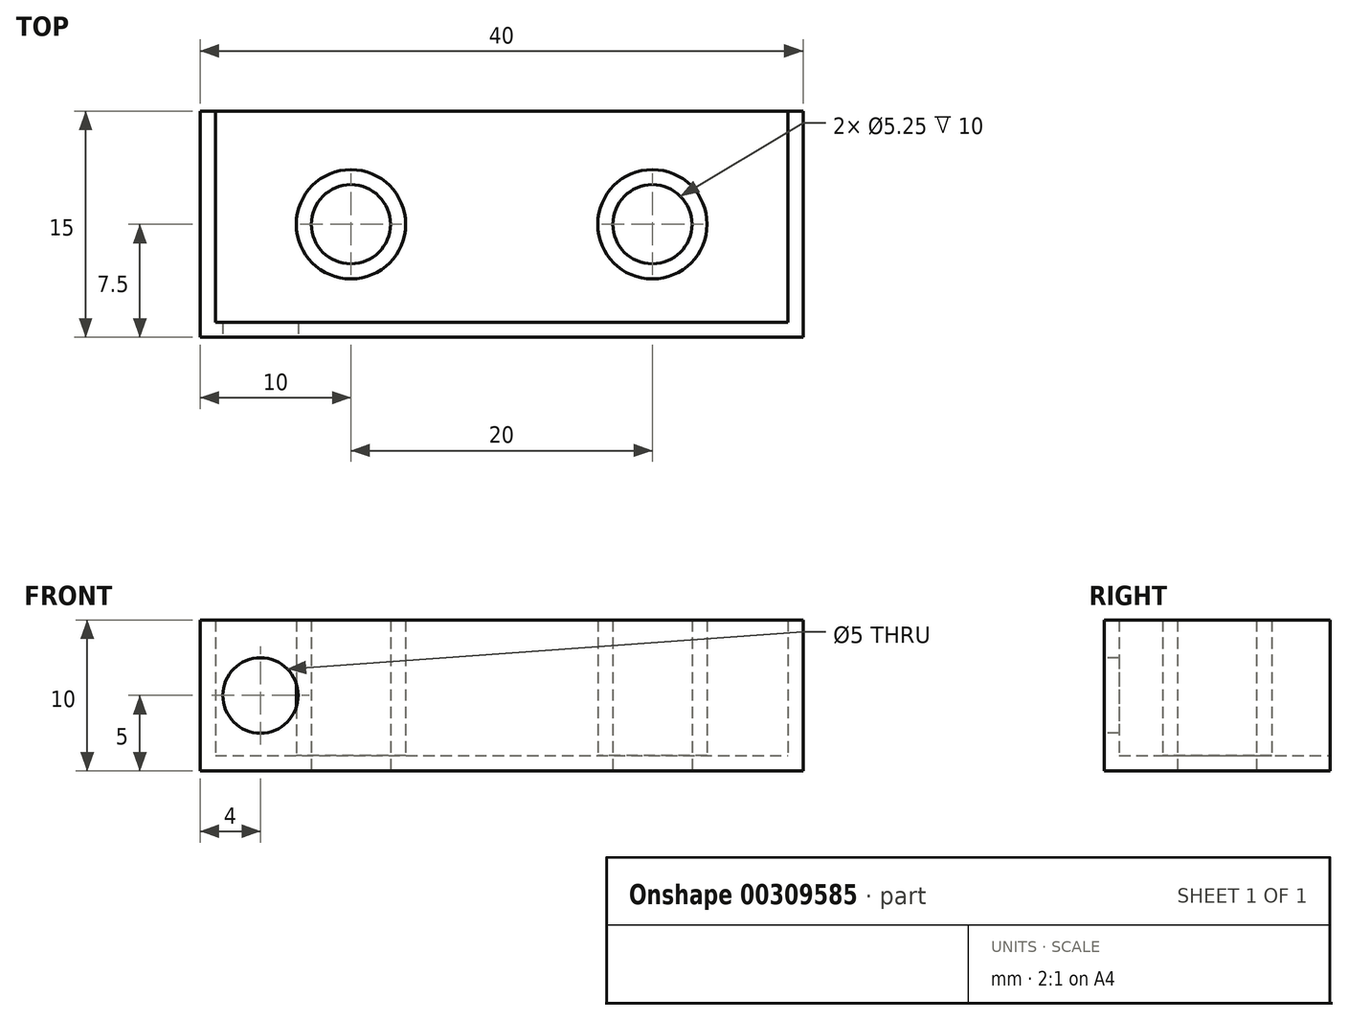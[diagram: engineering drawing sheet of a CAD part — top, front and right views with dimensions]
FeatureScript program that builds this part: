
annotation { "Feature Type Name" : "Feature", "Feature Type Description" : "" }
export const myFeature = defineFeature(function(context is Context, id is Id, definition is map)
    precondition{}
    {
        {
            var Q0;
            Q0=qCreatedBy(makeId("Top.planeOp"),FACE);
            var sketch = newSketch(context, id + "F0", { "sketchPlane" : qUnion([Q0])});
            skLineSegment(sketch, "E0.bottom", {"start": v(0, 0) * mm, "end": v(40, 0) * mm});
            skLineSegment(sketch, "E0.top", {"start": v(0, 15) * mm, "end": v(40, 15) * mm});
            skLineSegment(sketch, "E0.left", {"start": v(0, 0) * mm, "end": v(0, 15) * mm});
            skLineSegment(sketch, "E0.right", {"start": v(40, 0) * mm, "end": v(40, 15) * mm});
            skPoint(sketch, "E1", {"position": v(10, 7.5) * mm});
            skPoint(sketch, "E1.positionSnap0", {"position": v(0, 7.5) * mm});
            skPoint(sketch, "E2", {"position": v(30, 7.5) * mm});
            skSolve(sketch);
        }
        {
            var Q0;
            Q0=makeQuery(id+"F0.imprint","IMPRINT",FACE,{"disambiguationData":[TD([[makeQuery(id+"F0.imprint","IMPRINT",EDGE,{"derivedFrom":sQuery(id+"F0.wireOp",EDGE,"E0.bottom")}),1.0]])]});
            extrude(context, id + "F1", {"entities" : qUnion([Q0]), "depth" : 10 * mm, "offsetDistance" : 25 * mm});
        }
        {
            var Q0;
            Q0=sQuery(id+"F0.wireOp",VERTEX,"E1");
            var Q1;
            Q1=sQuery(id+"F0.wireOp",VERTEX,"E2");
            var Q2;
            Q2=makeQuery(id+"F1.opExtrude","SWEPT_BODY",BODY,{"disambiguationData":[OSD([sQuery(id+"F0.wireOp",EDGE,"E0.bottom"),sQuery(id+"F0.wireOp",EDGE,"E0.top"),sQuery(id+"F0.wireOp",EDGE,"E0.left"),sQuery(id+"F0.wireOp",EDGE,"E0.right")])]});
            hole(context, id + "F2", {"style" : HoleStyle.SIMPLE, "endStyle" : HoleEndStyle.THROUGH, "oppositeDirection" : true, "standardTappedOrClearance" : lookupTablePath({ "standard" : "ISO", "fit" : "Close", "size" : "M5", "type" : "Clearance" }), "standardBlindInLast" : lookupTablePath({ "fit" : "Close", "standard" : "ISO", "size" : "M5", "type" : "Clearance" }), "holeDiameter" : 5.25 * mm, "majorDiameter" : 5 * mm, "isTappedThrough" : true, "tappedDepth" : 12 * mm, "tapClearance" : 3, "startFromSketch" : true, "locations" : qUnion([Q0, Q1]), "scope" : qUnion([Q2])});
        }
        {
            var Q0;
            Q0=makeQuery(id+"F1.opExtrude","SWEPT_FACE",FACE,{"disambiguationData":[OSD([sQuery(id+"F0.wireOp",EDGE,"E0.top")])]});
            var Q1;
            Q1=makeQuery(id+"F1.opExtrude","CAP_FACE",FACE,{"disambiguationData":[OSD([sQuery(id+"F0.wireOp",EDGE,"E0.bottom"),sQuery(id+"F0.wireOp",EDGE,"E0.top"),sQuery(id+"F0.wireOp",EDGE,"E0.left"),sQuery(id+"F0.wireOp",EDGE,"E0.right")])],"isStart":false});
            shell(context, id + "F3", {"entities" : qUnion([Q0, Q1]), "thickness" : 1 * mm});
        }
        {
            var Q0;
            Q0=makeQuery(id+"F1.opExtrude","SWEPT_FACE",FACE,{"disambiguationData":[OSD([sQuery(id+"F0.wireOp",EDGE,"E0.bottom")])]});
            var sketch = newSketch(context, id + "F4", { "sketchPlane" : qUnion([Q0])});
            skLineSegment(sketch, "E3.bottom", {"start": v(35, 7.15) * mm, "end": v(38, 7.15) * mm});
            skLineSegment(sketch, "E3.top", {"start": v(35, 2.85) * mm, "end": v(38, 2.85) * mm});
            skLineSegment(sketch, "E3.left", {"start": v(35, 7.15) * mm, "end": v(35, 2.85) * mm});
            skLineSegment(sketch, "E3.right", {"start": v(38, 7.15) * mm, "end": v(38, 2.85) * mm});
            skPoint(sketch, "E3.middle", {"position": v(36.5, 5) * mm});
            skPoint(sketch, "E3.middle.positionSnap0", {"position": v(40, 5) * mm});
            skPoint(sketch, "E3.centerSnap0", {"position": v(40, 5) * mm});
            skPoint(sketch, "E4", {"position": v(4, 5) * mm});
            skSolve(sketch);
        }
        {
            var Q0;
            Q0=sQuery(id+"F4.wireOp",VERTEX,"E4");
            var Q1;
            Q1=makeQuery(id+"F1.opExtrude","SWEPT_BODY",BODY,{"disambiguationData":[OSD([sQuery(id+"F0.wireOp",EDGE,"E0.bottom"),sQuery(id+"F0.wireOp",EDGE,"E0.top"),sQuery(id+"F0.wireOp",EDGE,"E0.left"),sQuery(id+"F0.wireOp",EDGE,"E0.right")])]});
            hole(context, id + "F5", {"style" : HoleStyle.SIMPLE, "endStyle" : HoleEndStyle.BLIND, "holeDiameter" : 5 * mm, "majorDiameter" : 5 * mm, "holeDepth" : 2 * mm, "isTappedThrough" : true, "tappedDepth" : 12 * mm, "tapClearance" : 3, "startFromSketch" : true, "locations" : qUnion([Q0]), "scope" : qUnion([Q1])});
        }
    });
